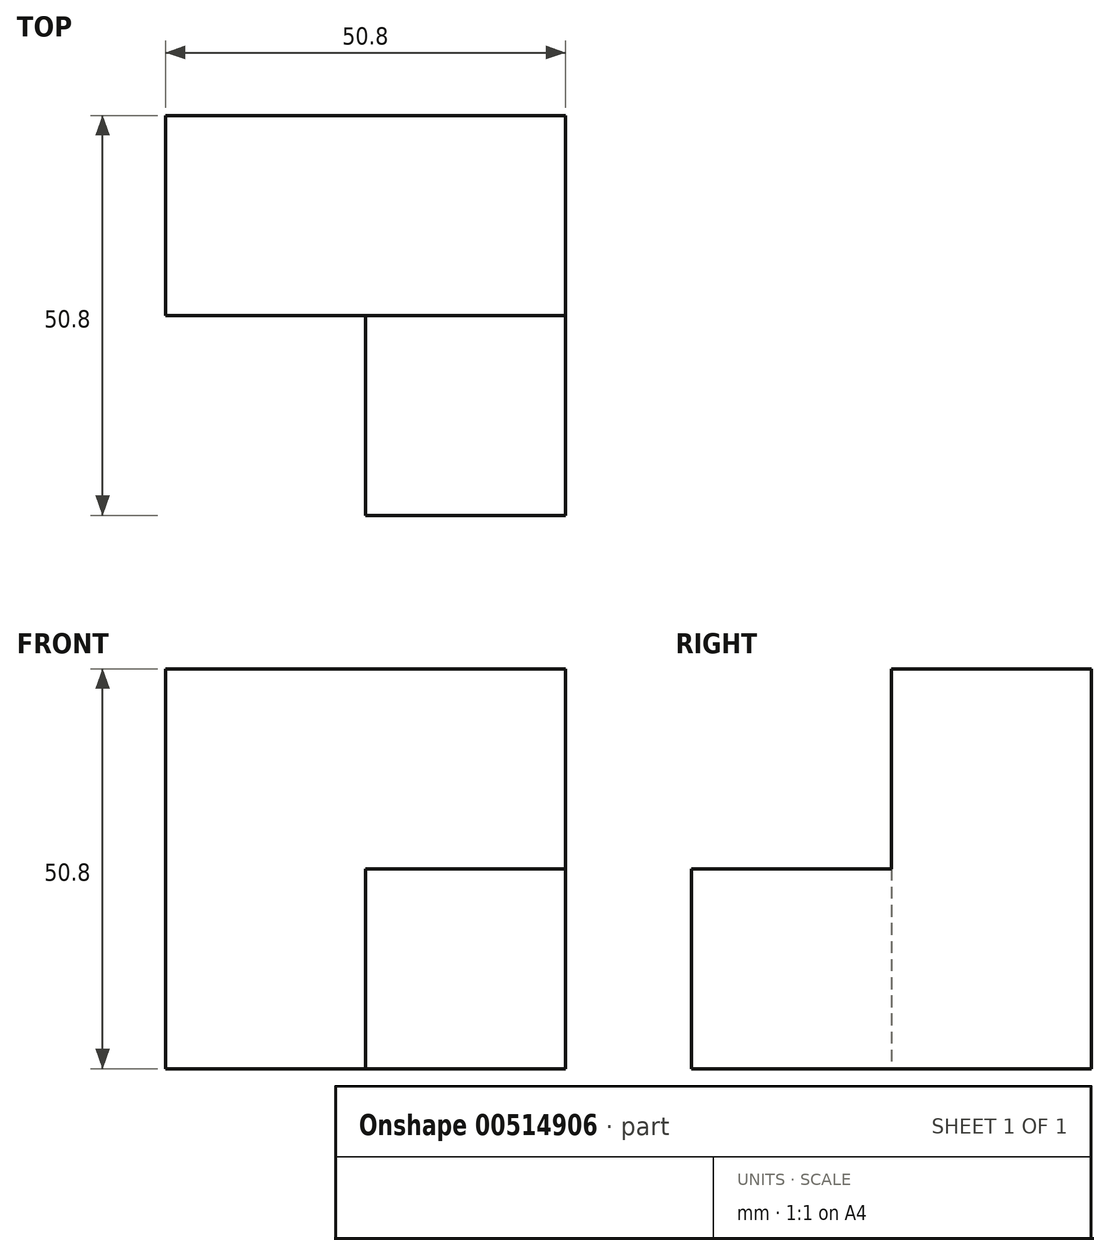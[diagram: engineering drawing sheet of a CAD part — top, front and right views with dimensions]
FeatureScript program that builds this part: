
annotation { "Feature Type Name" : "Feature", "Feature Type Description" : "" }
export const myFeature = defineFeature(function(context is Context, id is Id, definition is map)
    precondition{}
    {
        {
            var Q0;
            Q0=qCreatedBy(makeId("Front.planeOp"),FACE);
            var sketch = newSketch(context, id + "F0", { "sketchPlane" : qUnion([Q0])});
            skLineSegment(sketch, "E0.bottom", {"start": v(0, 0) * mm, "end": v(-50.8, 0) * mm});
            skLineSegment(sketch, "E0.top", {"start": v(0, 50.8) * mm, "end": v(-50.8, 50.8) * mm});
            skLineSegment(sketch, "E0.left", {"start": v(0, 0) * mm, "end": v(0, 50.8) * mm});
            skLineSegment(sketch, "E0.right", {"start": v(-50.8, 0) * mm, "end": v(-50.8, 50.8) * mm});
            skSolve(sketch);
        }
        {
            var Q0;
            Q0 = qSketchRegion(id + "F0", true);
            extrude(context, id + "F1", {"entities" : qUnion([Q0]), "depth" : 25.4 * mm, "offsetDistance" : 25.4 * mm});
        }
        {
            var Q0;
            Q0=qCreatedBy(makeId("Front.planeOp"),FACE);
            var sketch = newSketch(context, id + "F2", { "sketchPlane" : qUnion([Q0])});
            skLineSegment(sketch, "E1.bottom", {"start": v(0, 0) * mm, "end": v(-25.4, 0) * mm});
            skLineSegment(sketch, "E1.top", {"start": v(0, 25.4) * mm, "end": v(-25.4, 25.4) * mm});
            skLineSegment(sketch, "E1.left", {"start": v(0, 0) * mm, "end": v(0, 25.4) * mm});
            skLineSegment(sketch, "E1.right", {"start": v(-25.4, 0) * mm, "end": v(-25.4, 25.4) * mm});
            skSolve(sketch);
        }
        {
            var Q0;
            Q0 = qSketchRegion(id + "F2", true);
            extrude(context, id + "F3", {"entities" : qUnion([Q0]), "operationType" : NewBodyOperationType.ADD, "depth" : 25.4 * mm, "offsetDistance" : 25.4 * mm});
        }
        {
            var Q0;
            Q0=qCreatedBy(makeId("Front.planeOp"),FACE);
            var sketch = newSketch(context, id + "F4", { "sketchPlane" : qUnion([Q0])});
            skLineSegment(sketch, "E2.bottom", {"start": v(0, 0) * mm, "end": v(-25.4, 0) * mm});
            skLineSegment(sketch, "E2.top", {"start": v(0, 25.4) * mm, "end": v(-25.4, 25.4) * mm});
            skLineSegment(sketch, "E2.left", {"start": v(0, 0) * mm, "end": v(0, 25.4) * mm});
            skLineSegment(sketch, "E2.right", {"start": v(-25.4, 0) * mm, "end": v(-25.4, 25.4) * mm});
            skSolve(sketch);
        }
        {
            var Q0;
            Q0 = qSketchRegion(id + "F4", true);
            extrude(context, id + "F5", {"entities" : qUnion([Q0]), "operationType" : NewBodyOperationType.ADD, "depth" : 25.4 * mm, "offsetDistance" : 25.4 * mm});
        }
        {
            var Q0;
            Q0=qCreatedBy(makeId("Front.planeOp"),FACE);
            var sketch = newSketch(context, id + "F6", { "sketchPlane" : qUnion([Q0])});
            skLineSegment(sketch, "E3.bottom", {"start": v(0, 0) * mm, "end": v(-25.4, 0) * mm});
            skLineSegment(sketch, "E3.top", {"start": v(0, 25.4) * mm, "end": v(-25.4, 25.4) * mm});
            skLineSegment(sketch, "E3.left", {"start": v(0, 0) * mm, "end": v(0, 25.4) * mm});
            skLineSegment(sketch, "E3.right", {"start": v(-25.4, 0) * mm, "end": v(-25.4, 25.4) * mm});
            skSolve(sketch);
        }
        {
            var Q0;
            Q0 = qSketchRegion(id + "F6", true);
            extrude(context, id + "F7", {"entities" : qUnion([Q0]), "operationType" : NewBodyOperationType.ADD, "depth" : 25.4 * mm, "offsetDistance" : 25.4 * mm});
        }
        {
            var Q0;
            Q0=qCreatedBy(makeId("Front.planeOp"),FACE);
            var sketch = newSketch(context, id + "F8", { "sketchPlane" : qUnion([Q0])});
            skLineSegment(sketch, "E4.bottom", {"start": v(0, 0) * mm, "end": v(-25.4, 0) * mm});
            skLineSegment(sketch, "E4.top", {"start": v(0, 25.4) * mm, "end": v(-25.4, 25.4) * mm});
            skLineSegment(sketch, "E4.left", {"start": v(0, 0) * mm, "end": v(0, 25.4) * mm});
            skLineSegment(sketch, "E4.right", {"start": v(-25.4, 0) * mm, "end": v(-25.4, 25.4) * mm});
            skSolve(sketch);
        }
        {
            var Q0;
            Q0 = qSketchRegion(id + "F8", true);
            extrude(context, id + "F9", {"entities" : qUnion([Q0]), "operationType" : NewBodyOperationType.ADD, "depth" : 50.8 * mm, "offsetDistance" : 25.4 * mm});
        }
    });
